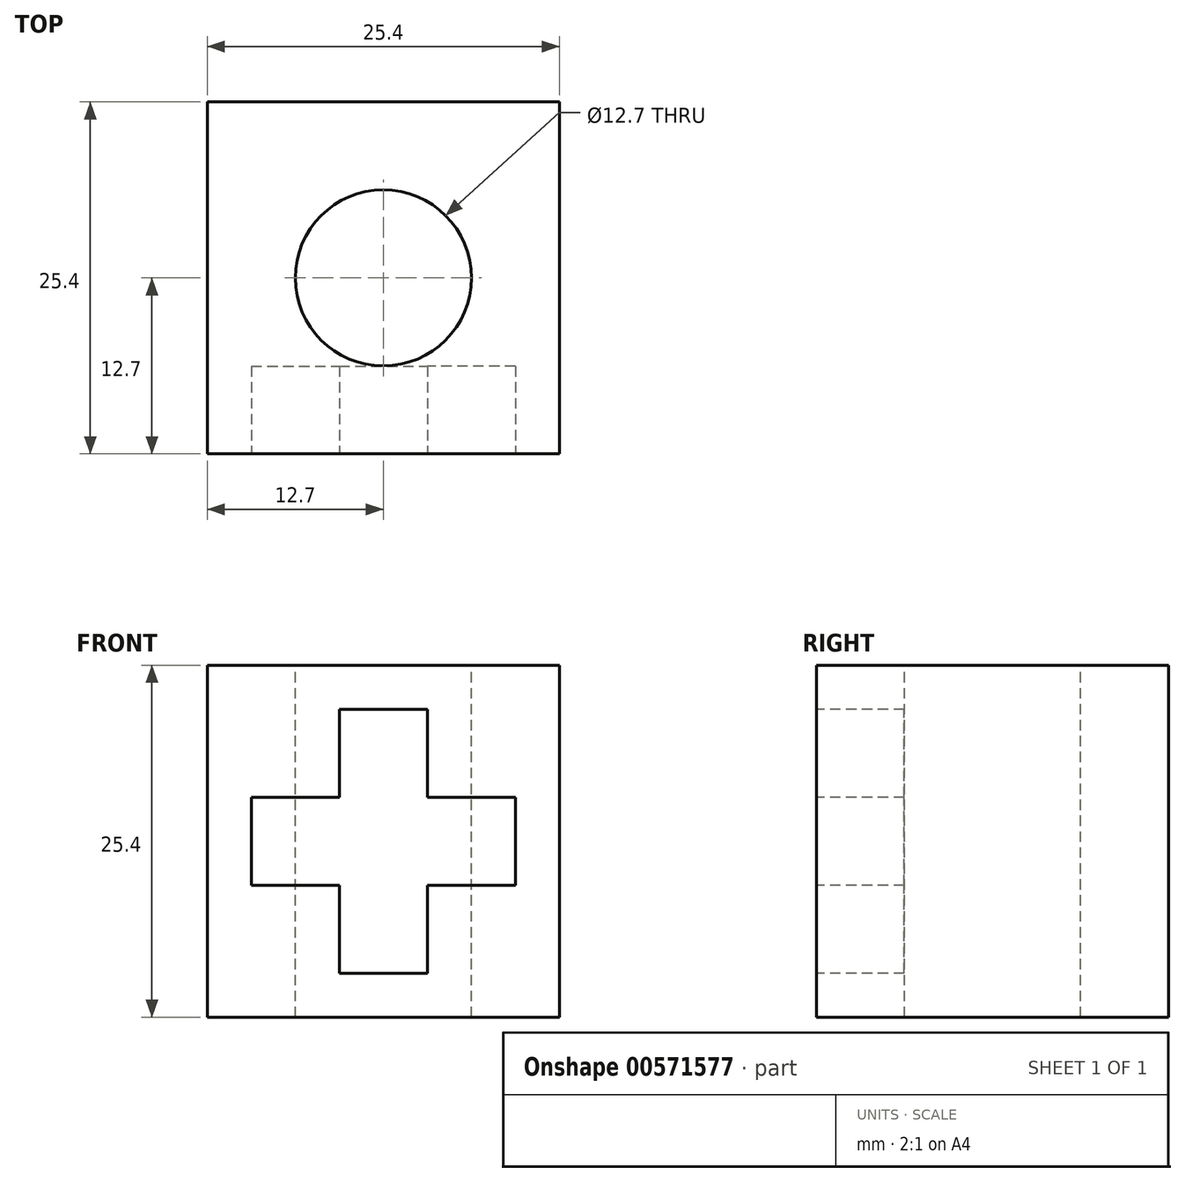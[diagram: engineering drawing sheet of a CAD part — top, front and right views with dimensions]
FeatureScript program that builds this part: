
annotation { "Feature Type Name" : "Feature", "Feature Type Description" : "" }
export const myFeature = defineFeature(function(context is Context, id is Id, definition is map)
    precondition{}
    {
        {
            var Q0;
            Q0=qCreatedBy(makeId("Front.planeOp"),FACE);
            var sketch = newSketch(context, id + "F0", { "sketchPlane" : qUnion([Q0])});
            skLineSegment(sketch, "E0", {"start": v(0, 0) * mm, "end": v(0, 25.4) * mm});
            skLineSegment(sketch, "E1", {"start": v(0, 25.4) * mm, "end": v(25.4, 25.4) * mm});
            skLineSegment(sketch, "E2", {"start": v(25.4, 25.4) * mm, "end": v(25.4, 0) * mm});
            skLineSegment(sketch, "E3", {"start": v(25.4, 0) * mm, "end": v(0, 0) * mm});
            skSolve(sketch);
        }
        {
            var Q0;
            Q0 = qSketchRegion(id + "F0", true);
            extrude(context, id + "F1", {"entities" : qUnion([Q0]), "endBound" : BoundingType.SYMMETRIC, "depth" : 25.4 * mm, "offsetDistance" : 25.4 * mm});
        }
        {
            var Q0;
            Q0=makeQuery(id+"F1.opExtrude","SWEPT_FACE",FACE,{"disambiguationData":[OSD([sQuery(id+"F0.wireOp",EDGE,"E1")])]});
            var sketch = newSketch(context, id + "F2", { "sketchPlane" : qUnion([Q0])});
            skLineSegment(sketch, "E4", {"start": v(0, 0) * mm, "end": v(25.4, 0) * mm, "construction": true});
            skCircle(sketch, "E5", {"center": v(12.7, 0) * mm, "radius": 6.35 * mm});
            skSolve(sketch);
        }
        {
            var Q0;
            Q0 = qSketchRegion(id + "F2", true);
            extrude(context, id + "F3", {"entities" : qUnion([Q0]), "operationType" : NewBodyOperationType.REMOVE, "endBound" : BoundingType.UP_TO_NEXT, "oppositeDirection" : true, "depth" : 25.4 * mm, "offsetDistance" : 25.4 * mm});
        }
        {
            var Q0;
            Q0=makeQuery(id+"F1.opExtrude","CAP_FACE",FACE,{"disambiguationData":[OSD([sQuery(id+"F0.wireOp",EDGE,"E0"),sQuery(id+"F0.wireOp",EDGE,"E1"),sQuery(id+"F0.wireOp",EDGE,"E2"),sQuery(id+"F0.wireOp",EDGE,"E3")])],"isStart":false});
            var sketch = newSketch(context, id + "F4", { "sketchPlane" : qUnion([Q0])});
            skLineSegment(sketch, "E6", {"start": v(12.7, 25.4) * mm, "end": v(12.7, 12.7) * mm, "construction": true});
            skLineSegment(sketch, "E7", {"start": v(12.7, 12.7) * mm, "end": v(12.7, 0) * mm, "construction": true});
            skLineSegment(sketch, "E8", {"start": v(9.53, 22.23) * mm, "end": v(15.88, 22.23) * mm});
            skLineSegment(sketch, "E9", {"start": v(15.88, 22.23) * mm, "end": v(15.88, 15.88) * mm});
            skLineSegment(sketch, "E10", {"start": v(15.88, 15.88) * mm, "end": v(22.23, 15.88) * mm});
            skLineSegment(sketch, "E11", {"start": v(22.23, 15.88) * mm, "end": v(22.23, 9.53) * mm});
            skLineSegment(sketch, "E12", {"start": v(22.23, 9.53) * mm, "end": v(15.88, 9.53) * mm});
            skLineSegment(sketch, "E13", {"start": v(15.88, 9.53) * mm, "end": v(15.88, 3.17) * mm});
            skLineSegment(sketch, "E14", {"start": v(15.88, 3.17) * mm, "end": v(9.52, 3.17) * mm});
            skLineSegment(sketch, "E15", {"start": v(9.52, 3.17) * mm, "end": v(9.52, 9.52) * mm});
            skLineSegment(sketch, "E16", {"start": v(9.52, 9.52) * mm, "end": v(3.17, 9.52) * mm});
            skLineSegment(sketch, "E17", {"start": v(3.17, 9.52) * mm, "end": v(3.17, 15.87) * mm});
            skLineSegment(sketch, "E18", {"start": v(3.17, 15.87) * mm, "end": v(9.53, 15.87) * mm});
            skLineSegment(sketch, "E19", {"start": v(9.53, 15.87) * mm, "end": v(9.53, 22.23) * mm});
            skLineSegment(sketch, "E20", {"start": v(15.88, 15.88) * mm, "end": v(12.7, 12.7) * mm, "construction": true});
            skLineSegment(sketch, "E21", {"start": v(9.52, 9.52) * mm, "end": v(12.7, 12.7) * mm, "construction": true});
            skLineSegment(sketch, "E22", {"start": v(12.7, 12.7) * mm, "end": v(9.53, 15.87) * mm, "construction": true});
            skLineSegment(sketch, "E23", {"start": v(12.7, 12.7) * mm, "end": v(15.88, 9.53) * mm, "construction": true});
            skSolve(sketch);
        }
        {
            var Q0;
            Q0=makeQuery(id+"F4.imprint","IMPRINT",FACE,{"disambiguationData":[TD([[makeQuery(id+"F4.imprint","IMPRINT",EDGE,{"derivedFrom":sQuery(id+"F4.wireOp",EDGE,"E8")}),-1.0]])]});
            var Q1;
            Q1=qCreatedBy(makeId("Top.planeOp"),FACE);
            var Q2;
            Q2=makeQuery(id+"F1.opExtrude","SWEPT_BODY",BODY,{"disambiguationData":[OSD([sQuery(id+"F0.wireOp",EDGE,"E0"),sQuery(id+"F0.wireOp",EDGE,"E1"),sQuery(id+"F0.wireOp",EDGE,"E2"),sQuery(id+"F0.wireOp",EDGE,"E3")])]});
            extrude(context, id + "F5", {"entities" : qUnion([Q0]), "operationType" : NewBodyOperationType.REMOVE, "oppositeDirection" : true, "depth" : 6.32 * mm, "endBoundEntityFace" : qUnion([Q1]), "endBoundEntityBody" : qUnion([Q2]), "offsetDistance" : 25.4 * mm});
        }
    });
